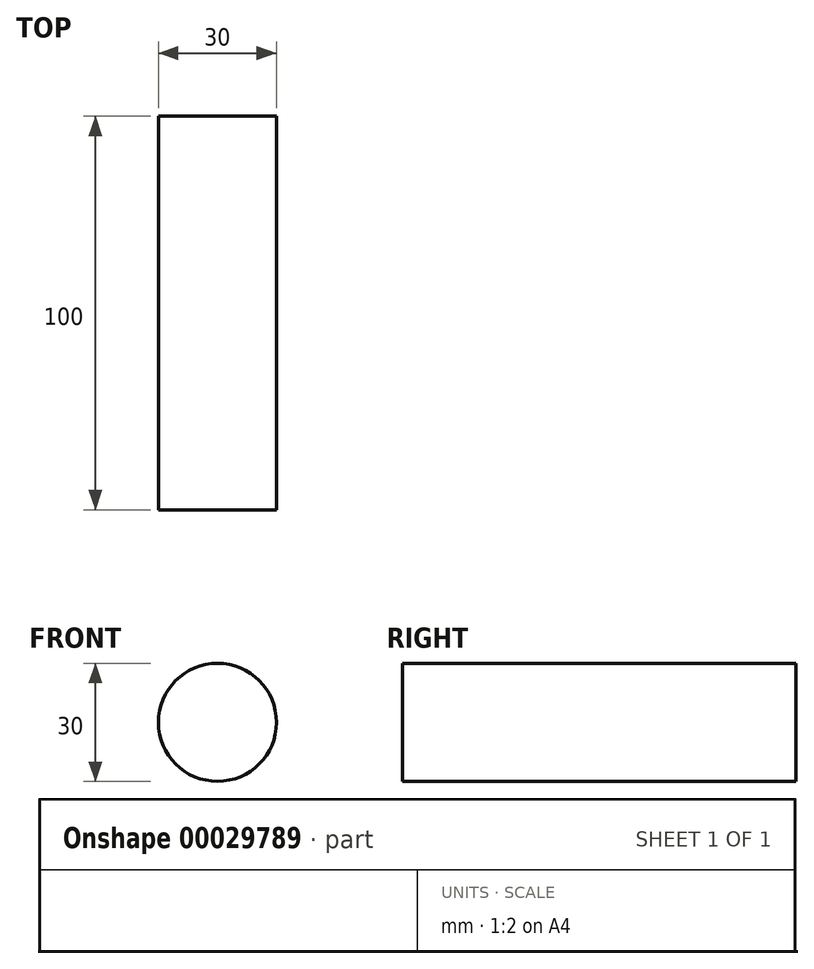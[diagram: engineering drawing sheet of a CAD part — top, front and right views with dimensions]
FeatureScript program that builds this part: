
annotation { "Feature Type Name" : "Feature", "Feature Type Description" : "" }
export const myFeature = defineFeature(function(context is Context, id is Id, definition is map)
    precondition{}
    {
        {
            var Q0;
            Q0=qCreatedBy(makeId("Front.planeOp"),FACE);
            var sketch = newSketch(context, id + "F0", { "sketchPlane" : qUnion([Q0])});
            skCircle(sketch, "E0", {"center": v(0, 0) * mm, "radius": 15 * mm});
            skSolve(sketch);
        }
        {
            var Q0;
            Q0=makeQuery(id+"F0.imprint","IMPRINT",FACE,{"disambiguationData":[TD([[makeQuery(id+"F0.imprint","IMPRINT",EDGE,{"derivedFrom":sQuery(id+"F0.wireOp",EDGE,"E0")}),1.0]])]});
            extrude(context, id + "F1", {"entities" : qUnion([Q0]), "depth" : 100 * mm});
        }
    });
